FCSTD DOCUMENT  (FreeCAD 0.20R29603 (Git))
Label: chair_measurements
License: Creative Commons Attribution
LicenseURL: http://creativecommons.org/licenses/by/4.0/
objects: PartDesign::Body×1, Sketcher::SketchObject×1
note: 2 computed .brp shape members not serialized (recipe doc carries the construction recipe); baked Part::Feature solids carry a one-line shape summary decoded from their .brp
EXTERNAL_REF file=chair_dimension_spreadsheet.FCStd obj=Spreadsheet

FEATURE [PartDesign::Body] Body
  Origin = -> Origin
FEATURE [Sketcher::SketchObject] Sketch001  label="Dimension Sketch"
  FullyConstrained = false
  MapMode = 5
  Placement = pos=(0,0,0) rot=(0.57735,0.57735,0.57735;2.0944rad)
  Support = -> [YZ_Plane]
  expr: Constraints[0] = <<chair_dimension_spreadsheet>>#<<dim_sheet>>.back_thickness
  expr: Constraints[13] = <<chair_dimension_spreadsheet>>#<<dim_sheet>>.leg_vertical_height
  expr: Constraints[19] = <<chair_dimension_spreadsheet>>#<<dim_sheet>>.cushion_thickness
  expr: Constraints[33] = <<chair_dimension_spreadsheet>>#<<dim_sheet>>.leg_thickness
  expr: Constraints[52] = <<chair_dimension_spreadsheet>>#<<dim_sheet>>.cushion_length
  expr: Constraints[53] = <<chair_dimension_spreadsheet>>#<<dim_sheet>>.leg_angle
  expr: Constraints[57] = <<chair_dimension_spreadsheet>>#<<dim_sheet>>.back_length
  expr: Constraints[9] = <<chair_dimension_spreadsheet>>#<<dim_sheet>>.back_angle
  sketch-geometry (23):
    g0: LineSegment StartX=287.015 StartY=25.4 StartZ=0 EndX=547.634 EndY=741.446 EndZ=0
    g1: LineSegment StartX=547.634 StartY=741.446 StartZ=0 EndX=595.37 EndY=724.071 EndZ=0
    g2: LineSegment StartX=595.37 StartY=724.071 StartZ=0 EndX=322.585 EndY=-25.4 EndZ=0
    g3: LineSegment StartX=287.015 StartY=25.4 StartZ=0 EndX=-322.585 EndY=25.4 EndZ=0
    g4: LineSegment StartX=-287.015 StartY=-25.4 StartZ=0 EndX=322.585 EndY=-25.4 EndZ=0
    g5: GeomPoint X=0 Y=0 Z=0
    g6: LineSegment StartX=-287.015 StartY=-25.4 StartZ=0 EndX=-397.953 EndY=-330.2 EndZ=0
    g7: LineSegment StartX=-397.953 StartY=-330.2 StartZ=0 EndX=-452.013 EndY=-330.2 EndZ=0
    g8: LineSegment StartX=-452.013 StartY=-330.2 StartZ=0 EndX=-322.585 EndY=25.4 EndZ=0
    g9: LineSegment StartX=-287.015 StartY=-25.4 StartZ=0 EndX=-268.525 EndY=25.4 EndZ=0
    g10: LineSegment StartX=-368.046 StartY=25.4 StartZ=0 EndX=-322.585 EndY=25.4 EndZ=0
    g11: LineSegment StartX=-316.261 StartY=42.7746 StartZ=0 EndX=-268.525 EndY=25.4 EndZ=0
    g12: LineSegment StartX=-268.525 StartY=25.4 StartZ=0 EndX=-404.277 EndY=-347.575 EndZ=0
    g13: LineSegment StartX=-404.277 StartY=-347.575 StartZ=0 EndX=-452.013 EndY=-330.2 EndZ=0
    g14: LineSegment StartX=-452.013 StartY=-330.2 StartZ=0 EndX=-316.261 EndY=42.7746 EndZ=0
    g15: LineSegment StartX=-341.075 StartY=-25.4 StartZ=0 EndX=341.075 EndY=-25.4 EndZ=0
    g16: LineSegment StartX=341.075 StartY=-25.4 StartZ=0 EndX=341.075 EndY=25.4 EndZ=0
    g17: LineSegment StartX=341.075 StartY=25.4 StartZ=0 EndX=-341.075 EndY=25.4 EndZ=0
    g18: LineSegment StartX=-341.075 StartY=25.4 StartZ=0 EndX=-341.075 EndY=-25.4 EndZ=0
    g19: LineSegment StartX=268.525 StartY=-25.4 StartZ=0 EndX=316.261 EndY=-42.7746 EndZ=0
    g20: LineSegment StartX=316.261 StartY=-42.7746 StartZ=0 EndX=595.37 EndY=724.071 EndZ=0
    g21: LineSegment StartX=595.37 StartY=724.071 StartZ=0 EndX=547.634 EndY=741.446 EndZ=0
    g22: LineSegment StartX=547.634 StartY=741.446 StartZ=0 EndX=268.525 EndY=-25.4 EndZ=0
  constraints (60):
    c: Distance(g1) = 50.8
    c: Coincident(g1,g0)
    c: Coincident(g2,g1)
    c: Parallel(g2,g0)
    c: Perpendicular(g1,g0)
    c: Coincident(g4,g2)
    c: PointOnObject(g5,g-1)
    c: PointOnObject(g5,g-2)
    c: Coincident(g3,g0)
    c: Angle(g0,g3) = 1.91986
    c: Coincident(g7,g8)
    c: Horizontal(g7)
    c: Parallel(g6,g8)
    c: DistanceY(g6,g6) = 304.8
    c: Tangent(g9,g6)
    c: PointOnObject(g9,g4)
    c: PointOnObject(g9,g3)
    c: Coincident(g6,g7)
    c: Coincident(g10,g3)
    c: DistanceY(g4,g9) = 50.8
    c: Horizontal(g4)
    c: Coincident(g8,g3)
    c: Coincident(g4,g6)
    c: Coincident(g11,g12)
    c: Coincident(g12,g13)
    c: Coincident(g13,g14)
    c: Coincident(g14,g11)
    c: Perpendicular(g11,g14)
    c: Parallel(g13,g11)
    c: Tangent(g14,g8)
    c: Tangent(g6,g12)
    c: Coincident(g13,g7)
    c: Coincident(g9,g11)
    c: Distance(g13) = 50.8
    c: Coincident(g15,g16)
    c: Coincident(g16,g17)
    c: Coincident(g17,g18)
    c: Coincident(g18,g15)
    c: Vertical(g18)
    c: Tangent(g17,g3)
    c: Tangent(g15,g4)
    c: PointOnObject(g15,g8)
    c: PointOnObject(g16,g2)
    c: Coincident(g19,g20)
    c: Coincident(g20,g21)
    c: Coincident(g21,g22)
    c: Coincident(g22,g19)
    c: Tangent(g22,g0)
    c: Tangent(g20,g2)
    c: Perpendicular(g22,g19)
    c: PointOnObject(g19,g4)
    c: Tangent(g21,g1)
    c: DistanceX(g3,g3) = 609.6
    c: Angle(g6,g4) = 1.91986
    c: Symmetric(g17,g16,g-2)
    c: Distance(g11,g7) = 396.911  'leg_cut_length'
    c: DistanceX(g17,g16) = 682.15  'cushion_cut_length'
    c: Distance(g0) = 762
    c: Distance(g19,g1) = 816.06  'back_cut_length'
    c: Symmetric(g16,g15,g-1)
